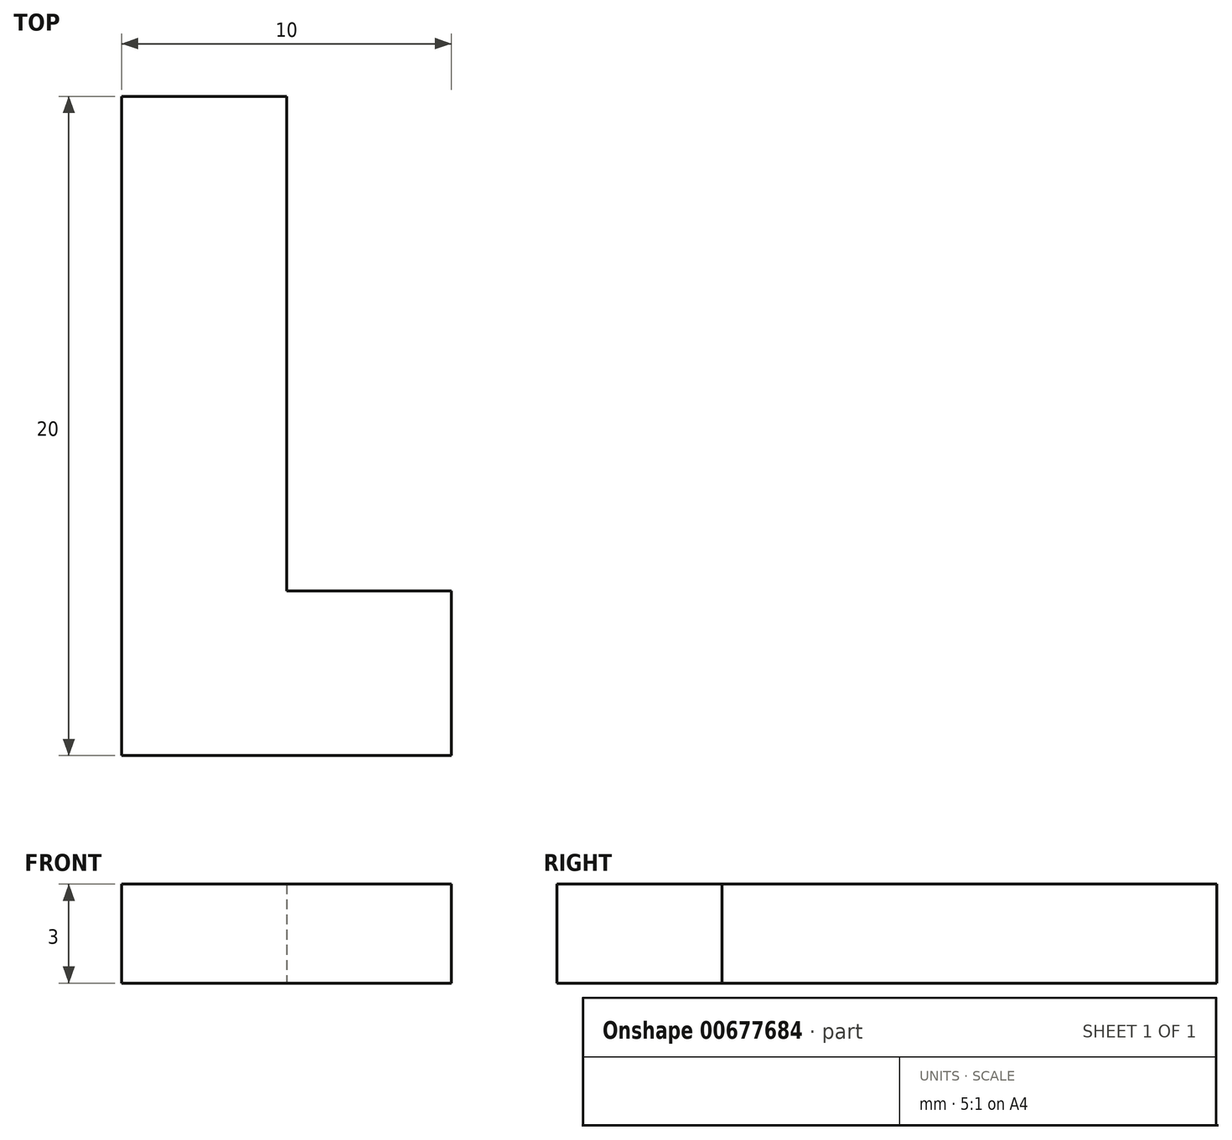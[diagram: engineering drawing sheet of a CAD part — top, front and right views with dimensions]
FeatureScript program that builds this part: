
annotation { "Feature Type Name" : "Feature", "Feature Type Description" : "" }
export const myFeature = defineFeature(function(context is Context, id is Id, definition is map)
    precondition{}
    {
        {
            var Q0;
            Q0=qCreatedBy(makeId("Top.planeOp"),FACE);
            var sketch = newSketch(context, id + "F0", { "sketchPlane" : qUnion([Q0])});
            skLineSegment(sketch, "E0", {"start": v(0, 20) * mm, "end": v(0, 0) * mm});
            skLineSegment(sketch, "E1", {"start": v(0, 0) * mm, "end": v(10, 0) * mm});
            skLineSegment(sketch, "E2", {"start": v(10, 0) * mm, "end": v(10, 5) * mm});
            skLineSegment(sketch, "E3", {"start": v(10, 5) * mm, "end": v(5, 5) * mm});
            skLineSegment(sketch, "E4", {"start": v(5, 5) * mm, "end": v(5, 20) * mm});
            skLineSegment(sketch, "E5", {"start": v(5, 20) * mm, "end": v(0, 20) * mm});
            skSolve(sketch);
        }
        {
            var Q0;
            Q0 = qSketchRegion(id + "F0", true);
            extrude(context, id + "F1", {"entities" : qUnion([Q0]), "depth" : 3 * mm, "offsetDistance" : 25 * mm});
        }
    });
